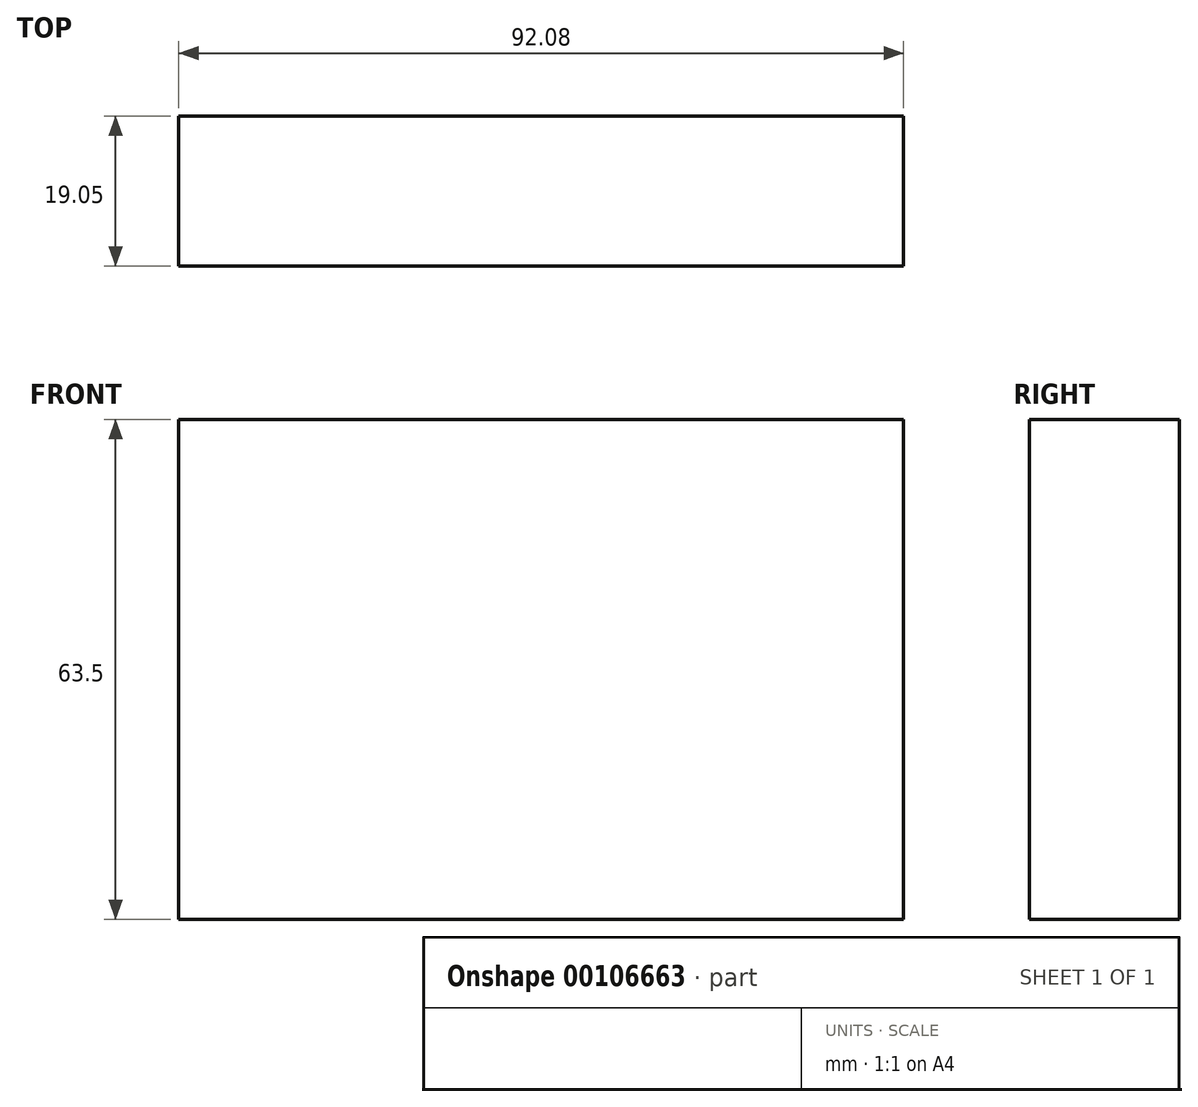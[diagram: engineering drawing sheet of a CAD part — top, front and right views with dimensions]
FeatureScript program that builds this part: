
annotation { "Feature Type Name" : "Feature", "Feature Type Description" : "" }
export const myFeature = defineFeature(function(context is Context, id is Id, definition is map)
    precondition{}
    {
        {
            var Q0;
            Q0=qCreatedBy(makeId("Front.planeOp"),FACE);
            var sketch = newSketch(context, id + "F0", { "sketchPlane" : qUnion([Q0])});
            skLineSegment(sketch, "E0.bottom", {"start": v(0, 0) * mm, "end": v(92.07, 0) * mm});
            skLineSegment(sketch, "E0.top", {"start": v(0, 63.5) * mm, "end": v(92.07, 63.5) * mm});
            skLineSegment(sketch, "E0.left", {"start": v(0, 0) * mm, "end": v(0, 63.5) * mm});
            skLineSegment(sketch, "E0.right", {"start": v(92.07, 0) * mm, "end": v(92.07, 63.5) * mm});
            skSolve(sketch);
        }
        {
            var Q0;
            Q0=makeQuery(id+"F0.imprint","IMPRINT",FACE,{"disambiguationData":[TD([[makeQuery(id+"F0.imprint","IMPRINT",EDGE,{"derivedFrom":sQuery(id+"F0.wireOp",EDGE,"E0.bottom")}),1.0]])]});
            extrude(context, id + "F1", {"entities" : qUnion([Q0]), "depth" : 19.05 * mm});
        }
    });
